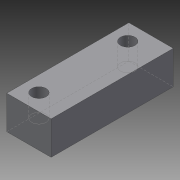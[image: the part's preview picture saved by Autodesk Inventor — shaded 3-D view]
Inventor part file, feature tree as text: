
AUTODESK INVENTOR PART (.ipt)
format: ipt  version: 2015 (Build 190159000, 159)  size: 87,552 bytes
history: native  units: mm
features: extrude x2, sketch x2
ambient origin geometry x8: Origin, YZ Plane, XZ Plane, XY Plane, X Axis, Y Axis, Z Axis, Center Point
bodies: Solid1 (feature_tree)
feature tree (4):
  extrude  "Extrusion1"  Depth=20.0mm
  extrude  "Extrusion2"  Depth=10.0mm
  sketch  "Sketch1"  dims[d0=55.0mm d1=20.0mm]
  sketch  "Sketch2"  dims[d2=15.0mm d3=0.0mm d4=40.0mm d5=7.5mm d6=7.0mm d7=7.5mm d8=6.5mm d9=6.5mm d10=10.0mm d11=0.0mm]
